# Revit family: SG
name_source: partatom
category: Lighting Fixtures
revit_build: Autodesk Revit 2013 (Build: 20130531_2115(x64)
units: mm (PartAtom-declared; Revit-internal decimal feet)

## types (5) — shared parameters
Apparent Load = 20 VA
Assembly Code = D5020200
Description = Perimeter wall or flood illumination
Glass = Hubbell-White Glass
Lamp = LED
Load Classification = Lighting
Manufacturer = Hubbell Outdoor Lighting
Manufacturer Fax = 866-898-1065
Model = SG Sling
Power Factor = 1
Product Documentation Link = http://cdn.hubbelloutdoor.com
Product Page URL = http://www.hubbelloutdoor.com
URL = http://www.hubbelloutdoor.com
Voltage = 120 V
Wattage Comments = 20, 30, 50,& 80W

## per-type parameters (varying)
| type | Box Finish | Photometric Web | Product Option |
| SG-BL | Hubbell-Textured Black | Web SG : SG2-50-3K-PCU | Sling Series : SG2 |
| SG-DB | Hubbell-Textured Dark Bronze | Web SG : SG1-20-PCU | Sling Series : SG2 |
| SG-WH | Hubbell-Textured White | Web SG : SG1-20-PCU | Sling Series : SG1 |
| SG-GYS | Hubbell-Smooth Gray | Web SG : SG1-20-PCU | Sling Series : SG2 |
| SG-PS | Hubbell-Platinum | Web SG : SG1-20-PCU | Sling Series : SG1 |

## geometry (parser evidence)
native form markers: Blend x2, Sweep x8
no freeform markers — native parametric forms only
